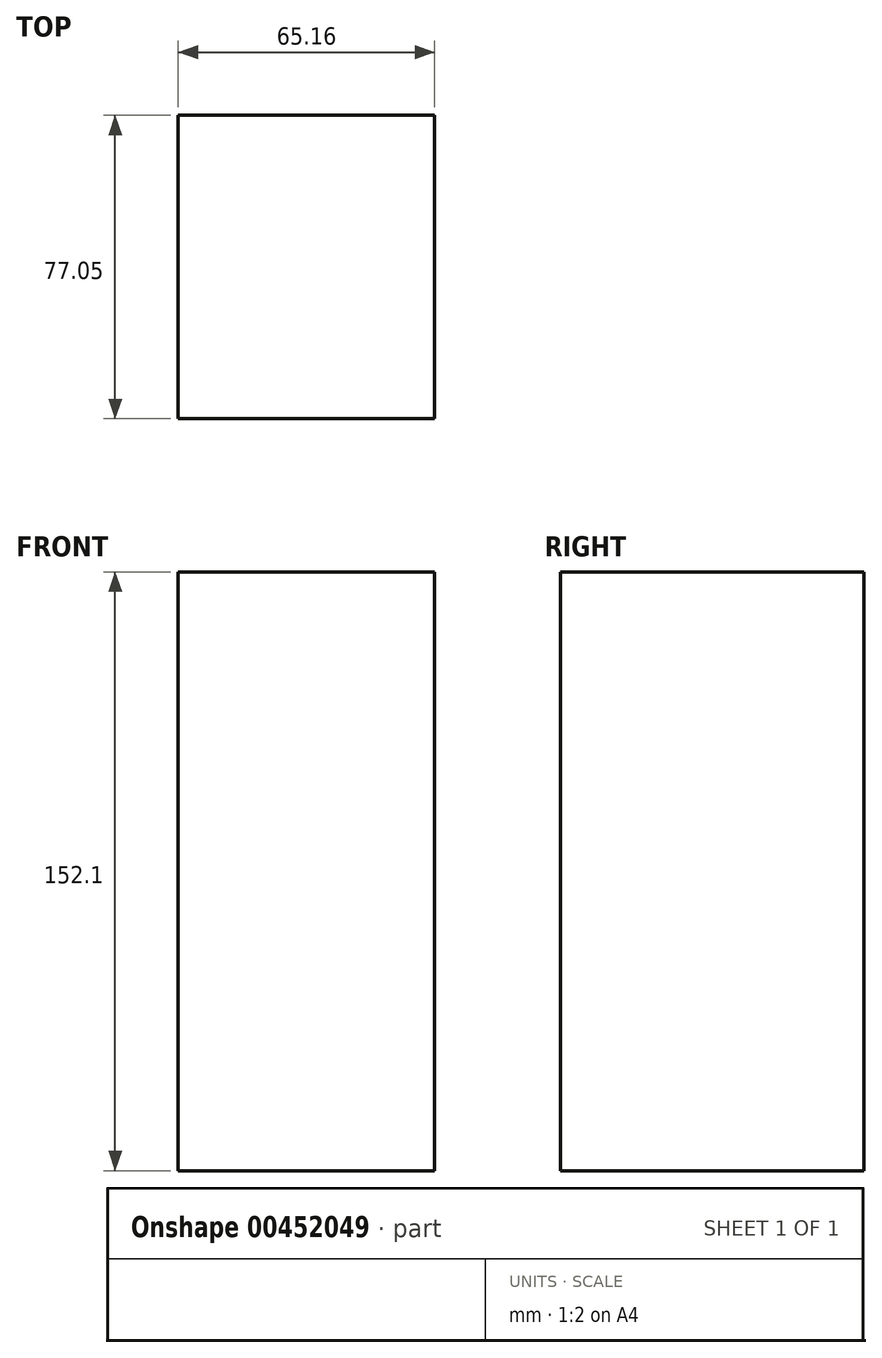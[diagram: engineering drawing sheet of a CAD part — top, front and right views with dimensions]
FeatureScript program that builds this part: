
annotation { "Feature Type Name" : "Feature", "Feature Type Description" : "" }
export const myFeature = defineFeature(function(context is Context, id is Id, definition is map)
    precondition{}
    {
        {
            var Q0;
            Q0=qCreatedBy(makeId("Right.planeOp"),FACE);
            var sketch = newSketch(context, id + "F0", { "sketchPlane" : qUnion([Q0])});
            skLineSegment(sketch, "E0.bottom", {"start": v(0, -79.5) * mm, "end": v(-77.05, -79.5) * mm});
            skLineSegment(sketch, "E0.top", {"start": v(0, 72.61) * mm, "end": v(-77.05, 72.61) * mm});
            skLineSegment(sketch, "E0.left", {"start": v(0, -79.5) * mm, "end": v(0, 72.61) * mm});
            skLineSegment(sketch, "E0.right", {"start": v(-77.05, -79.5) * mm, "end": v(-77.05, 72.61) * mm});
            skSolve(sketch);
        }
        {
            var Q0;
            Q0=makeQuery(id+"F0.imprint","IMPRINT",FACE,{"disambiguationData":[TD([[makeQuery(id+"F0.imprint","IMPRINT",EDGE,{"derivedFrom":sQuery(id+"F0.wireOp",EDGE,"E0.bottom")}),-1.0]])]});
            extrude(context, id + "F1", {"entities" : qUnion([Q0]), "oppositeDirection" : true, "depth" : 65.16 * mm});
        }
    });
